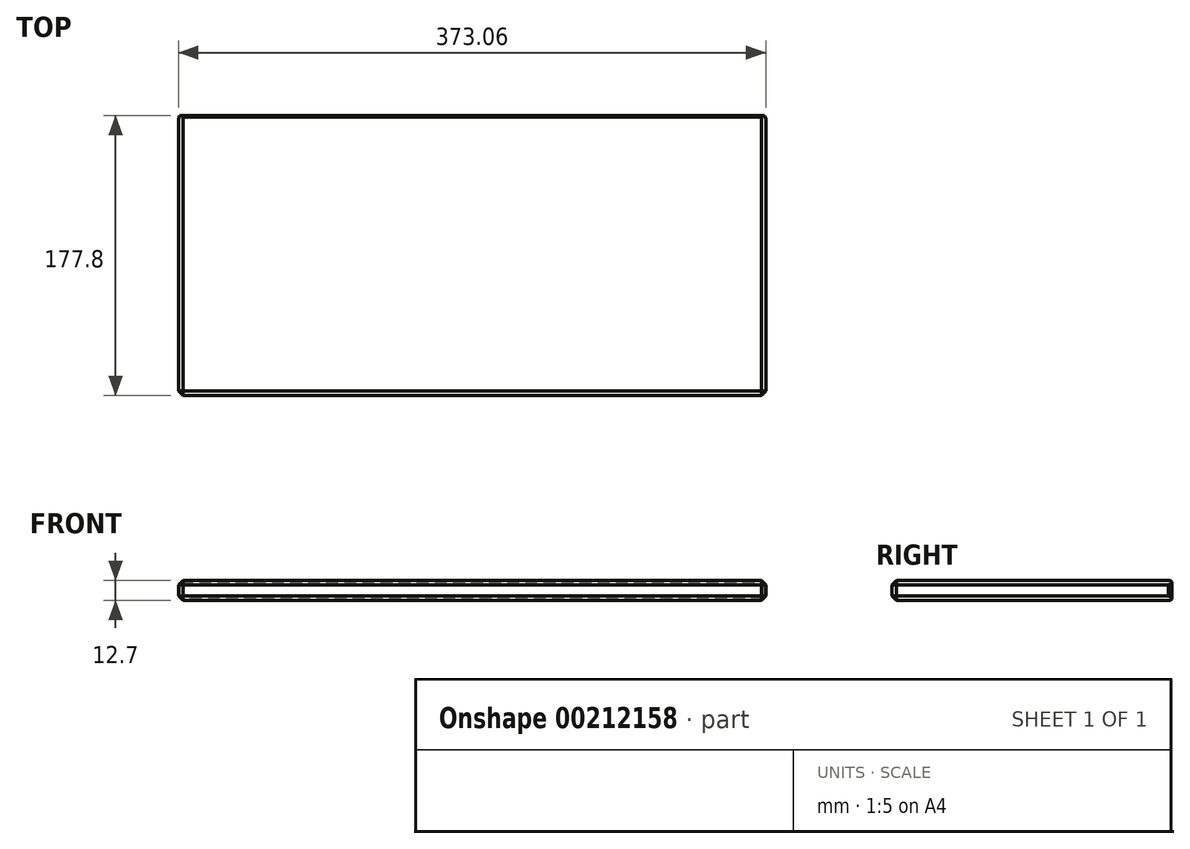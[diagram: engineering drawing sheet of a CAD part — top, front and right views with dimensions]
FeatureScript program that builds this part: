
annotation { "Feature Type Name" : "Feature", "Feature Type Description" : "" }
export const myFeature = defineFeature(function(context is Context, id is Id, definition is map)
    precondition{}
    {
        {
            var Q0;
            Q0=qCreatedBy(makeId("Top.planeOp"),FACE);
            var sketch = newSketch(context, id + "F0", { "sketchPlane" : qUnion([Q0])});
            skLineSegment(sketch, "E0.bottom", {"start": v(-186.53, 88.9) * mm, "end": v(186.53, 88.9) * mm});
            skLineSegment(sketch, "E0.top", {"start": v(-186.53, -88.9) * mm, "end": v(186.53, -88.9) * mm});
            skLineSegment(sketch, "E0.left", {"start": v(-186.53, 88.9) * mm, "end": v(-186.53, -88.9) * mm});
            skLineSegment(sketch, "E0.right", {"start": v(186.53, 88.9) * mm, "end": v(186.53, -88.9) * mm});
            skPoint(sketch, "E0.middle", {"position": v(0, 0) * mm});
            skSolve(sketch);
        }
        {
            var Q0;
            Q0=makeQuery(id+"F0.imprint","IMPRINT",FACE,{"disambiguationData":[TD([[makeQuery(id+"F0.imprint","IMPRINT",EDGE,{"derivedFrom":sQuery(id+"F0.wireOp",EDGE,"E0.bottom")}),-1.0]])]});
            extrude(context, id + "F1", {"entities" : qUnion([Q0]), "depth" : 12.7 * mm});
        }
        {
            var Q0;
            Q0=makeQuery(id+"F1.opExtrude","SWEPT_FACE",FACE,{"disambiguationData":[OSD([sQuery(id+"F0.wireOp",EDGE,"E0.bottom")])]});
            chamfer(context, id + "F2", {"entities" : qUnion([Q0]), "width" : 1.02 * mm, "tangentPropagation" : true});
        }
        {
            var Q0;
            Q0=makeQuery(id+"F1.opExtrude","SWEPT_FACE",FACE,{"disambiguationData":[OSD([sQuery(id+"F0.wireOp",EDGE,"E0.left")])]});
            var Q1;
            Q1=makeQuery(id+"F1.opExtrude","SWEPT_FACE",FACE,{"disambiguationData":[OSD([sQuery(id+"F0.wireOp",EDGE,"E0.top")])]});
            var Q2;
            Q2=makeQuery(id+"F1.opExtrude","SWEPT_FACE",FACE,{"disambiguationData":[OSD([sQuery(id+"F0.wireOp",EDGE,"E0.right")])]});
            chamfer(context, id + "F3", {"entities" : qUnion([Q0, Q1, Q2]), "width" : 2.86 * mm, "tangentPropagation" : true});
        }
    });
